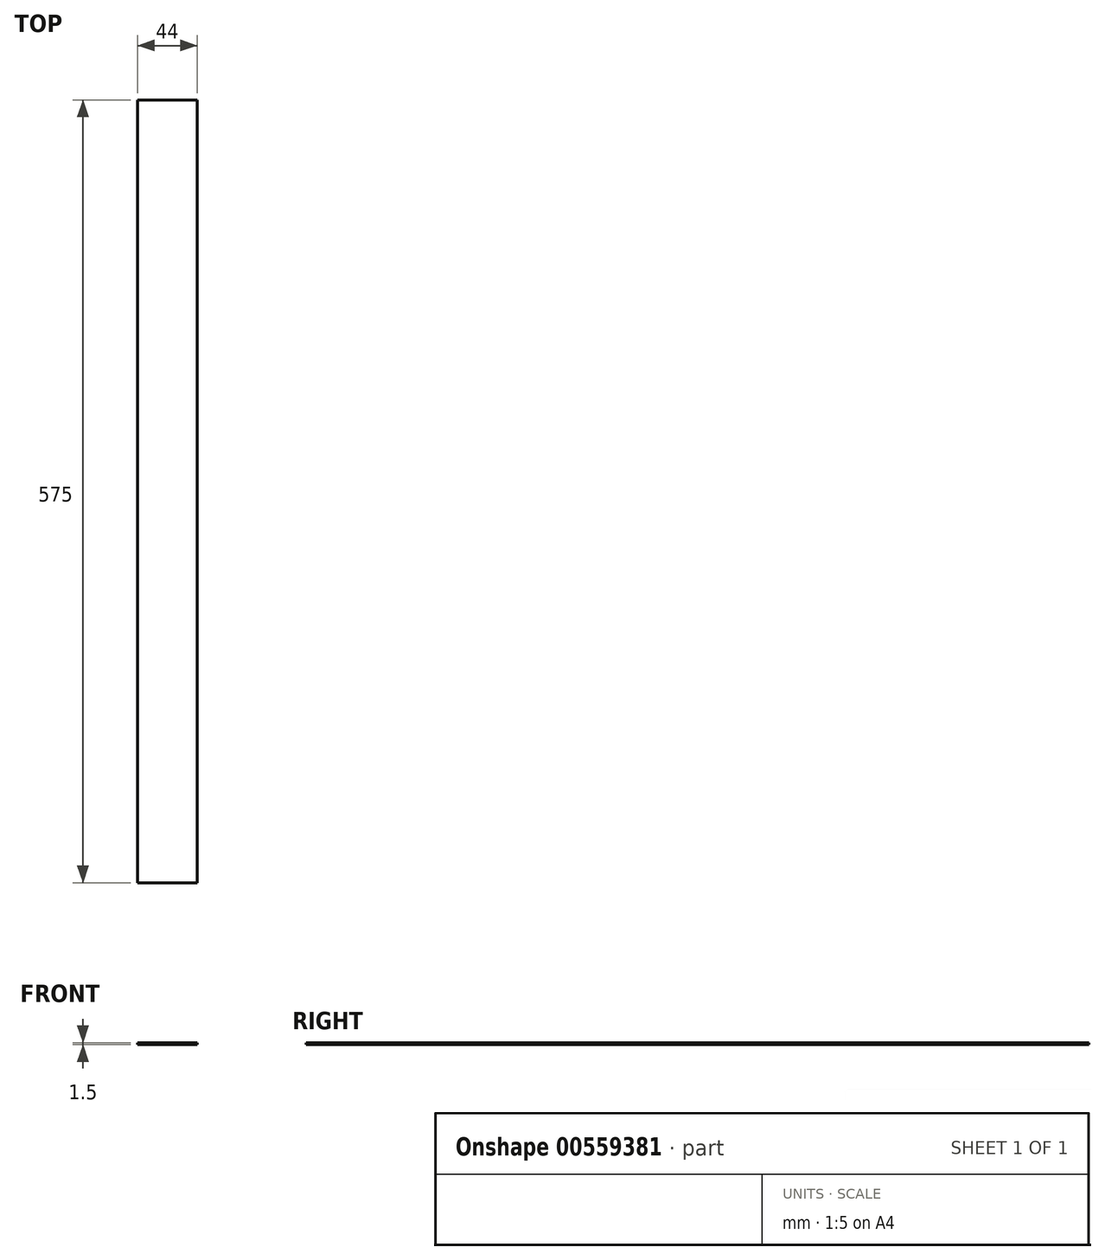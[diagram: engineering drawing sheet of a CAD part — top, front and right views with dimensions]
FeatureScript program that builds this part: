
annotation { "Feature Type Name" : "Feature", "Feature Type Description" : "" }
export const myFeature = defineFeature(function(context is Context, id is Id, definition is map)
    precondition{}
    {
        {
            var Q0;
            Q0=qCreatedBy(makeId("Front.planeOp"),FACE);
            var sketch = newSketch(context, id + "F0", { "sketchPlane" : qUnion([Q0])});
            skLineSegment(sketch, "E0", {"start": v(0, 0) * mm, "end": v(44, 0) * mm});
            skLineSegment(sketch, "E1", {"start": v(44, 0) * mm, "end": v(44, -1.5) * mm});
            skLineSegment(sketch, "E2", {"start": v(44, -1.5) * mm, "end": v(0, -1.5) * mm});
            skLineSegment(sketch, "E3", {"start": v(0, -1.5) * mm, "end": v(0, 0) * mm});
            skSolve(sketch);
        }
        {
            var Q0;
            Q0 = qSketchRegion(id + "F0", true);
            extrude(context, id + "F1", {"entities" : qUnion([Q0]), "depth" : 575 * mm, "offsetDistance" : 25 * mm});
        }
    });
